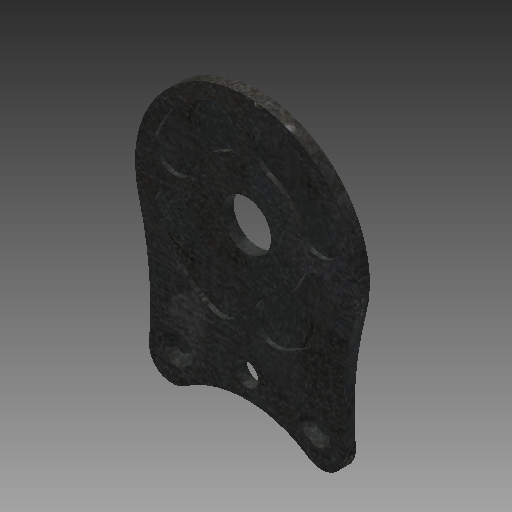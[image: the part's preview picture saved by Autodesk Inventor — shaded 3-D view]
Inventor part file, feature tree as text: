
AUTODESK INVENTOR PART (.ipt)
format: ipt  version: 2019 (Build 230136000, 136)  size: 347,648 bytes
history: native  units: mm
features: extrude x5, sketch x5, chamfer x2, mirror x2, fillet x1, pattern_circular x1, projected_geometry x1
ambient origin geometry x8: Origin, YZ Plane, XZ Plane, XY Plane, X Axis, Y Axis, Z Axis, Center Point
bodies: Solid1 (feature_tree)
feature tree (17):
  extrude  "Extrusion1"  Depth=78.0mm
  extrude  "Extrusion2"  Depth=26.125mm
  chamfer  "Chamfer1"  Distance=4.0mm
  mirror  "Mirror1"
  extrude  "Extrusion3"  Depth=6.75mm
  chamfer  "Chamfer2"  Angle=60.0deg  [1 undecoded]
  mirror  "Mirror2"
  extrude  "Extrusion4"  Depth=2.5mm
  extrude  "Extrusion5"  Depth=6.75mm
  fillet  "Fillet1"  Radius=49.35mm
  pattern_circular  "Circular Pattern1"  Angle=60.0deg  [1 undecoded]
  sketch  "Sketch1"  dims[d0=16.0mm d2=78.0mm]
  sketch  "Sketch2"  dims[d3=52.85mm d5=26.125mm]
  sketch  "Sketch3"  dims[d8=317.290738mm]
  projected_geometry  "Projected Loop1"
  sketch  "Sketch4"  dims[d9=26.125mm]
  sketch  "Sketch5"  dims[d10=38.035038mm d11=4.0mm d12=0.0mm d13=10.471976mm d14=60.0deg d15=2.5mm d16=22.825mm d17=49.35mm d18=60.0deg d19=1.95mm d20=2.5mm d21=0.0mm d22=2.5mm d23=2.0mm d24=45.0deg d25=2.5mm d26=0.0mm d27=2.5mm d28=2.0mm d29=45.0deg d30=1.75mm d31=17.0mm d32=45.0mm d33=8.0mm d34=2.5mm d35=0.0mm d36=68.0mm d37=40.0mm d38=2.5mm d39=2.8mm d40=1.5mm d41=0.0mm d42=6.75mm d43=40.0mm d44=360.0deg]
note: 2 required parameter values undecoded (feature->parameter linkage not recoverable at this tier; creation-order binding heuristic only, values carry confidence <= 0.55)
